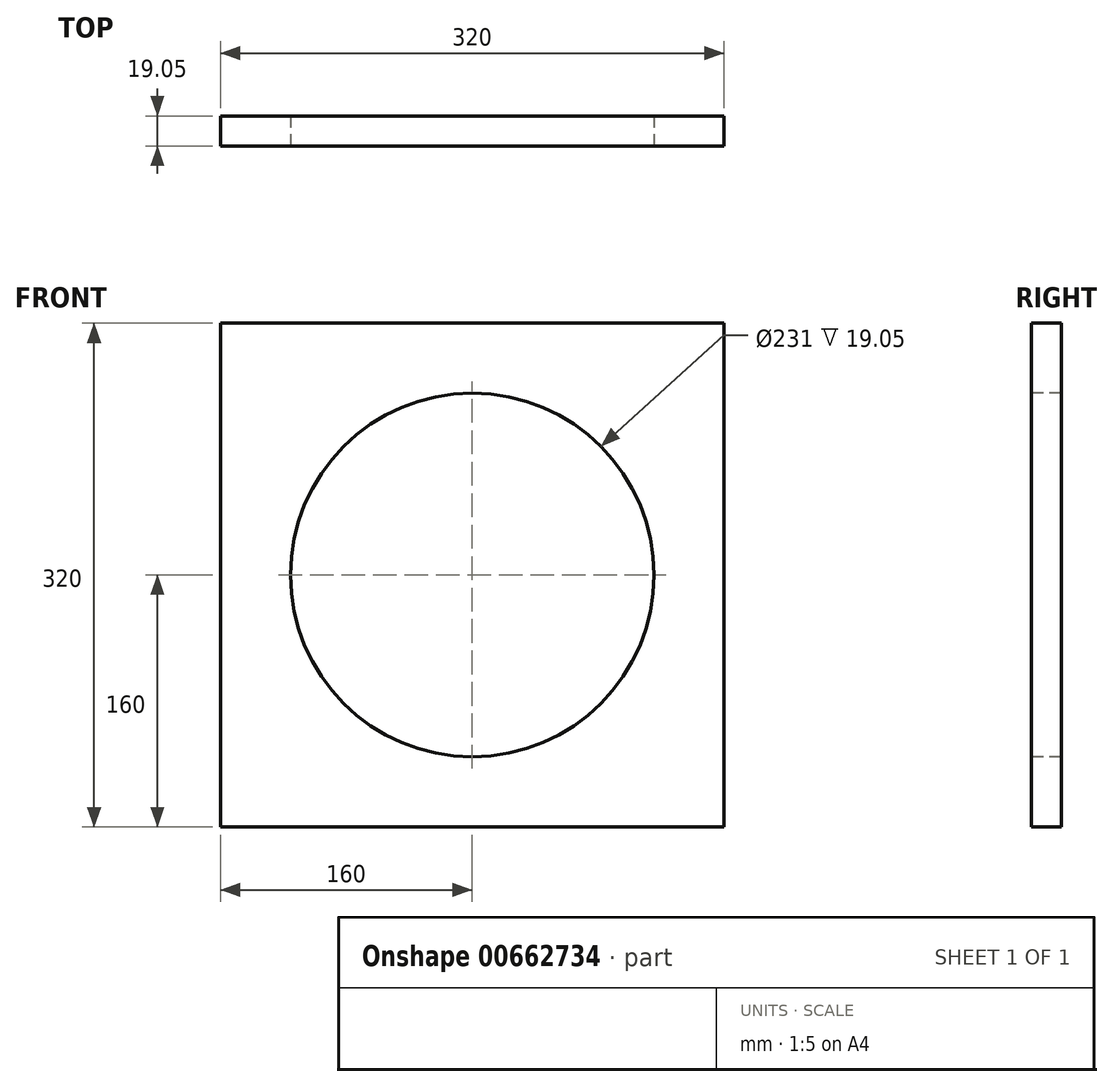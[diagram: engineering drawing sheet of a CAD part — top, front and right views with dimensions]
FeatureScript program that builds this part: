
annotation { "Feature Type Name" : "Feature", "Feature Type Description" : "" }
export const myFeature = defineFeature(function(context is Context, id is Id, definition is map)
    precondition{}
    {
        {
            var Q0;
            Q0=qCreatedBy(makeId("Front.planeOp"),FACE);
            var sketch = newSketch(context, id + "F0", { "sketchPlane" : qUnion([Q0])});
            skLineSegment(sketch, "E0.bottom", {"start": v(160, 160) * mm, "end": v(-160, 160) * mm});
            skLineSegment(sketch, "E0.top", {"start": v(160, -160) * mm, "end": v(-160, -160) * mm});
            skLineSegment(sketch, "E0.left", {"start": v(160, 160) * mm, "end": v(160, -160) * mm});
            skLineSegment(sketch, "E0.right", {"start": v(-160, 160) * mm, "end": v(-160, -160) * mm});
            skPoint(sketch, "E0.middle", {"position": v(0, 0) * mm});
            skCircle(sketch, "E1", {"center": v(0, 0) * mm, "radius": 115.5 * mm});
            skSolve(sketch);
        }
        {
            var Q0;
            Q0=makeQuery(id+"F0.imprint","IMPRINT",FACE,{"disambiguationData":[TD([[makeQuery(id+"F0.imprint","IMPRINT",EDGE,{"derivedFrom":sQuery(id+"F0.wireOp",EDGE,"E0.bottom")}),1.0]])]});
            extrude(context, id + "F1", {"entities" : qUnion([Q0]), "oppositeDirection" : true, "depth" : (25.4 * .75) * mm, "offsetDistance" : 25 * mm});
        }
    });
